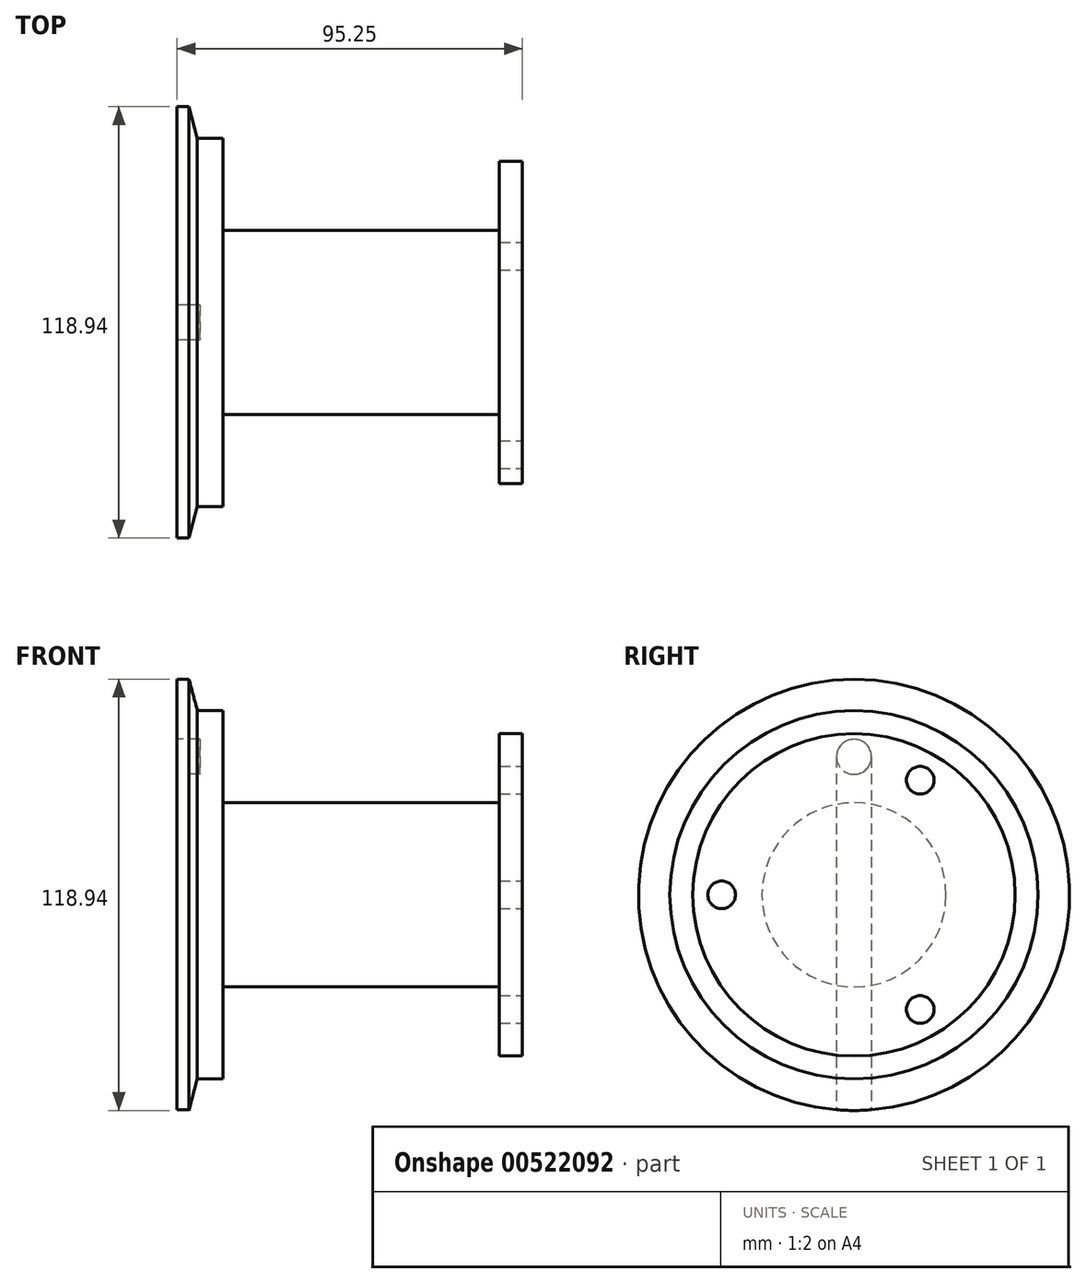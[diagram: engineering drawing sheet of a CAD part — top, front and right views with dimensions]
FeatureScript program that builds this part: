
annotation { "Feature Type Name" : "Feature", "Feature Type Description" : "" }
export const myFeature = defineFeature(function(context is Context, id is Id, definition is map)
    precondition{}
    {
        {
            var Q0;
            Q0=qCreatedBy(makeId("Front.planeOp"),FACE);
            var sketch = newSketch(context, id + "F0", { "sketchPlane" : qUnion([Q0])});
            skLineSegment(sketch, "E0", {"start": v(-116.46, 0) * mm, "end": v(101.28, 0) * mm, "construction": true});
            skLineSegment(sketch, "E1", {"start": v(0, 0) * mm, "end": v(0, 59.47) * mm});
            skLineSegment(sketch, "E2", {"start": v(0, 59.47) * mm, "end": v(3.3, 59.47) * mm});
            skLineSegment(sketch, "E3", {"start": v(0, 0) * mm, "end": v(12.7, 0) * mm});
            skLineSegment(sketch, "E4", {"start": v(12.7, 0) * mm, "end": v(12.7, 50.8) * mm});
            skLineSegment(sketch, "E5", {"start": v(12.7, 50.8) * mm, "end": v(5.63, 50.8) * mm});
            skLineSegment(sketch, "E6", {"start": v(3.3, 59.47) * mm, "end": v(5.63, 50.8) * mm});
            skSolve(sketch);
        }
        {
            var Q0;
            Q0 = qSketchRegion(id + "F0", true);
            var Q1;
            Q1=sQuery(id+"F0.wireOp",EDGE,"E0");
            revolve(context, id + "F1", {"entities" : qUnion([Q0]), "axis" : qUnion([Q1]), "revolveType" : RevolveType.FULL});
        }
        {
            var Q0;
            Q0=qCreatedBy(makeId("Right.planeOp"),FACE);
            var sketch = newSketch(context, id + "F2", { "sketchPlane" : qUnion([Q0])});
            skArc(sketch, "E7", {"start": v(4.83, 38.1) * mm, "mid": v(0, 42.93) * mm, "end": v(-4.83, 38.1) * mm});
            skLineSegment(sketch, "E8", {"start": v(4.83, 38.1) * mm, "end": v(4.83, -62.65) * mm});
            skLineSegment(sketch, "E9", {"start": v(4.83, -62.65) * mm, "end": v(-4.83, -62.65) * mm});
            skLineSegment(sketch, "E10", {"start": v(-4.83, 38.1) * mm, "end": v(-4.83, -62.65) * mm});
            skSolve(sketch);
        }
        {
            var Q0;
            Q0 = qSketchRegion(id + "F2", true);
            extrude(context, id + "F3", {"entities" : qUnion([Q0]), "operationType" : NewBodyOperationType.REMOVE, "depth" : 3.3 * mm, "offsetDistance" : 25.4 * mm});
        }
        {
            var Q0;
            Q0=qCreatedBy(makeId("Right.planeOp"),FACE);
            var sketch = newSketch(context, id + "F4", { "sketchPlane" : qUnion([Q0])});
            skCircle(sketch, "E11", {"center": v(0, 38.1) * mm, "radius": 4.83 * mm});
            skSolve(sketch);
        }
        {
            var Q0;
            Q0 = qSketchRegion(id + "F4", true);
            extrude(context, id + "F5", {"entities" : qUnion([Q0]), "operationType" : NewBodyOperationType.REMOVE, "depth" : 6.35 * mm, "offsetDistance" : 25.4 * mm});
        }
        {
            var Q0;
            Q0=makeQuery(id+"F1.opRevolve","SWEPT_FACE",FACE,{"disambiguationData":[OSD([sQuery(id+"F0.wireOp",EDGE,"E4")])]});
            var sketch = newSketch(context, id + "F6", { "sketchPlane" : qUnion([Q0])});
            skCircle(sketch, "E12", {"center": v(0, 0) * mm, "radius": 25.4 * mm});
            skSolve(sketch);
        }
        {
            var Q0;
            Q0 = qSketchRegion(id + "F6", true);
            extrude(context, id + "F7", {"entities" : qUnion([Q0]), "operationType" : NewBodyOperationType.ADD, "depth" : 76.2 * mm, "offsetDistance" : 25.4 * mm});
        }
        {
            var Q0;
            Q0=makeQuery(id+"F7.opExtrude","CAP_FACE",FACE,{"disambiguationData":[OSD([sQuery(id+"F6.wireOp",EDGE,"E12")])],"isStart":false});
            var sketch = newSketch(context, id + "F8", { "sketchPlane" : qUnion([Q0])});
            skCircle(sketch, "E13", {"center": v(0, 0) * mm, "radius": 44.45 * mm});
            skSolve(sketch);
        }
        {
            var Q0;
            Q0 = qSketchRegion(id + "F8", true);
            extrude(context, id + "F9", {"entities" : qUnion([Q0]), "operationType" : NewBodyOperationType.ADD, "depth" : 6.35 * mm, "offsetDistance" : 25.4 * mm});
        }
        {
            var Q0;
            Q0=makeQuery(id+"F9.opExtrude","CAP_FACE",FACE,{"disambiguationData":[OSD([sQuery(id+"F8.wireOp",EDGE,"E13")])],"isStart":false});
            var sketch = newSketch(context, id + "F10", { "sketchPlane" : qUnion([Q0])});
            skCircle(sketch, "E14", {"center": v(0, 0) * mm, "radius": 36.51 * mm, "construction": true});
            skCircle(sketch, "E15", {"center": v(-36.51, 0) * mm, "radius": 3.81 * mm});
            skCircle(sketch, "E16.1.0", {"center": v(18.26, -31.62) * mm, "radius": 3.81 * mm});
            skCircle(sketch, "E16.2.0", {"center": v(18.26, 31.62) * mm, "radius": 3.81 * mm});
            skSolve(sketch);
        }
        {
            var Q0;
            Q0 = qSketchRegion(id + "F10", true);
            extrude(context, id + "F11", {"entities" : qUnion([Q0]), "operationType" : NewBodyOperationType.REMOVE, "oppositeDirection" : true, "depth" : 25.4 * mm, "offsetDistance" : 25.4 * mm});
        }
    });
